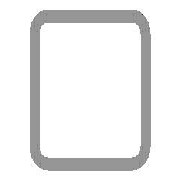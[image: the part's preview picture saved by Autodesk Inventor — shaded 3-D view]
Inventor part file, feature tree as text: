
AUTODESK INVENTOR PART (.ipt)
format: ipt  version: 2025 (Build 290162010, 162A)  size: 133,120 bytes
history: native  units: mm (DEFAULTED — no unit token found)
features: other x4, sketch x1, plane x1
ambient origin geometry x8: Origin, YZ Plane, XZ Plane, XY Plane, X Axis, Y Axis, Z Axis, Center Point
bodies: Solid1 (feature_tree), Body (feature_tree)
feature tree (6):
  parser-record x1  (decoder bookkeeping rows leaked as tree rows — omitted from the tree; the rows remain in map.json)
  other  "Driven Length"
  other  "Start Plane"
  other  "End Plane"
  sketch  "Sketch3"  dims[d3=780.0mm d4=0.0mm d7=8.0mm d9=50.0mm d11=50.0mm d12=4.0mm d13=-0.0mm d14=780.0mm d15=25.0mm d16=25.0mm d17=90.0deg d18=780.0mm]
  plane  "Work Plane3"
